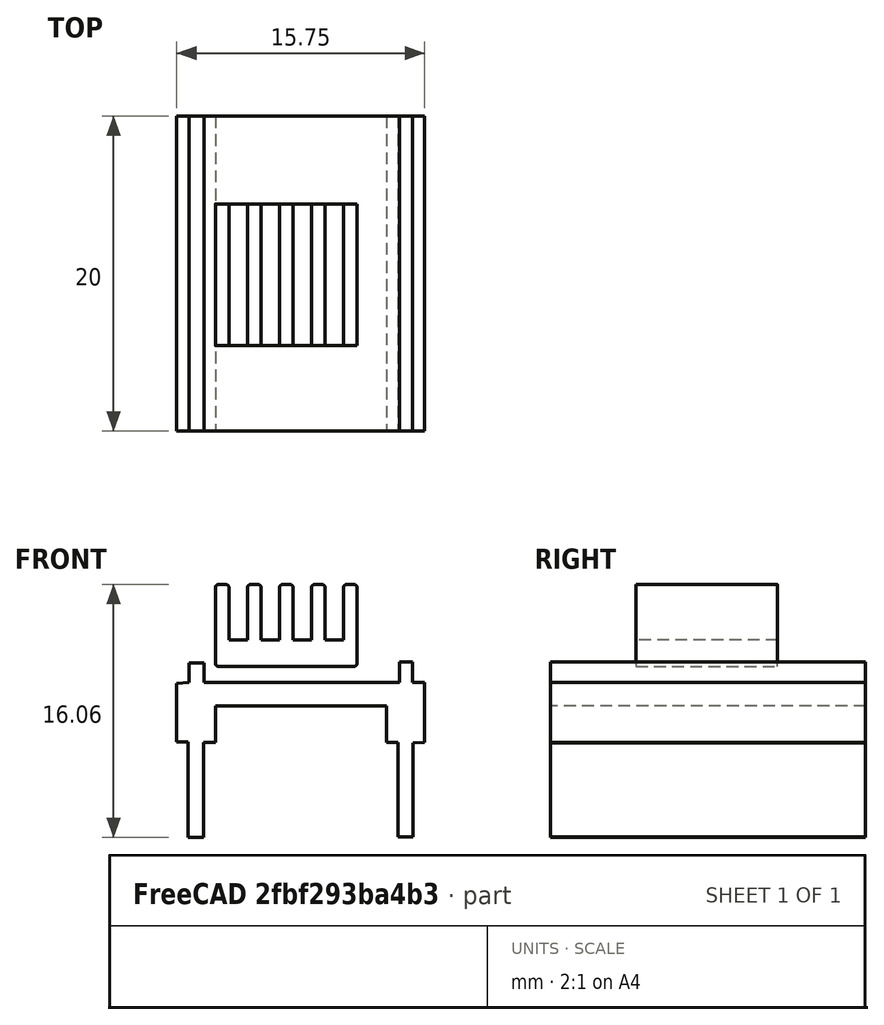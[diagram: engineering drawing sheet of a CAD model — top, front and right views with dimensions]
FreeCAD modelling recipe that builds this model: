
FCSTD DOCUMENT  (FreeCAD 0.16R6712 (Git))
Label: stepper
License: All rights reserved
LicenseURL: http://en.wikipedia.org/wiki/All_rights_reserved
objects: Part::Feature×1, Sketcher::SketchObject×1, PartDesign::Pad×1
note: 4 computed .brp shape members not serialized (recipe doc carries the construction recipe); baked Part::Feature solids carry a one-line shape summary decoded from their .brp

FEATURE [Part::Feature] Part__Feature034  label="Heat_Sink"
  Placement = pos=(-0.910921,-0.0804702,2.5) rot=(1,0,0;1.5708rad)
  shape: bbox 9 x 9 x 5.2 mm, 34 faces (baked)
FEATURE [Sketcher::SketchObject] Sketch
  Placement = pos=(0,0,0) rot=(-1,0,0;4.71239rad)
  sketch-geometry (25):
    g0: LineSegment StartX=-7.08984 StartY=2.70448 StartZ=0 EndX=-6.1315 EndY=2.70448 EndZ=0
    g1: LineSegment StartX=-6.1315 StartY=2.70448 StartZ=0 EndX=-6.1315 EndY=1.46643 EndZ=0
    g2: LineSegment StartX=-6.1315 StartY=1.46643 StartZ=0 EndX=6.27586 EndY=1.46643 EndZ=0
    g3: LineSegment StartX=6.27586 StartY=1.46643 StartZ=0 EndX=6.27586 EndY=2.77624 EndZ=0
    g4: LineSegment StartX=6.27586 StartY=2.77624 StartZ=0 EndX=7.1047 EndY=2.77624 EndZ=0
    g5: LineSegment StartX=7.1047 StartY=2.77624 StartZ=0 EndX=7.1047 EndY=1.47627 EndZ=0
    g6: LineSegment StartX=7.1047 StartY=1.47627 StartZ=0 EndX=7.8755 EndY=1.47627 EndZ=0
    g7: LineSegment StartX=7.8755 StartY=1.47627 StartZ=0 EndX=7.8755 EndY=-2.32364 EndZ=0
    g8: LineSegment StartX=7.8755 StartY=-2.32364 StartZ=0 EndX=7.12437 EndY=-2.36364 EndZ=0
    g9: LineSegment StartX=7.12437 StartY=-2.36364 StartZ=0 EndX=7.12437 EndY=-8.33415 EndZ=0
    g10: LineSegment StartX=7.12437 StartY=-8.33415 StartZ=0 EndX=6.19695 EndY=-8.31415 EndZ=0
    g11: LineSegment StartX=6.19695 StartY=-8.31415 StartZ=0 EndX=6.19695 EndY=-2.33428 EndZ=0
    g12: LineSegment StartX=6.19695 StartY=-2.33428 StartZ=0 EndX=5.44583 EndY=-2.33428 EndZ=0
    g13: LineSegment StartX=5.44583 StartY=-2.33428 StartZ=0 EndX=5.44583 EndY=0 EndZ=0
    g14: LineSegment StartX=5.44583 StartY=0 StartZ=0 EndX=-5.38959 EndY=0 EndZ=0
    g15: LineSegment StartX=-5.38959 StartY=0 StartZ=0 EndX=-5.38959 EndY=-2.33799 EndZ=0
    g16: LineSegment StartX=-5.38959 StartY=-2.33799 StartZ=0 EndX=-6.15088 EndY=-2.33799 EndZ=0
    g17: LineSegment StartX=-6.15088 StartY=-2.33799 StartZ=0 EndX=-6.15088 EndY=-8.35674 EndZ=0
    g18: LineSegment StartX=-6.15088 StartY=-8.35674 StartZ=0 EndX=-7.14748 EndY=-8.35674 EndZ=0
    g19: LineSegment StartX=-7.14748 StartY=-8.35674 StartZ=0 EndX=-7.14748 EndY=-2.30704 EndZ=0
    g20: LineSegment StartX=-7.14748 StartY=-2.30704 StartZ=0 EndX=-7.86844 EndY=-2.30704 EndZ=0
    g21: LineSegment StartX=-7.86844 StartY=-2.30704 StartZ=0 EndX=-7.86844 EndY=1.41435 EndZ=0
    g22: LineSegment StartX=-7.86844 StartY=1.41435 StartZ=0 EndX=-7.08172 EndY=1.46938 EndZ=0
    g23: LineSegment StartX=-7.08172 StartY=1.46938 StartZ=0 EndX=-7.08984 EndY=2.70448 EndZ=0
    g24: LineSegment StartX=-7.08984 StartY=2.70448 StartZ=0 EndX=-6.1315 EndY=2.70448 EndZ=0
  constraints (47):
    c: Coincident(g0,g1)
    c: Vertical(g1)
    c: Coincident(g1,g2)
    c: Horizontal(g2)
    c: Coincident(g2,g3)
    c: Vertical(g3)
    c: Coincident(g3,g4)
    c: Horizontal(g4)
    c: Coincident(g4,g5)
    c: Vertical(g5)
    c: Coincident(g5,g6)
    c: Horizontal(g6)
    c: Coincident(g6,g7)
    c: Vertical(g7)
    c: Coincident(g7,g8)
    c: Coincident(g8,g9)
    c: Vertical(g9)
    c: Coincident(g9,g10)
    c: Coincident(g10,g11)
    c: Vertical(g11)
    c: Coincident(g11,g12)
    c: Horizontal(g12)
    c: Coincident(g12,g13)
    c: PointOnObject(g13,g-1)
    c: Vertical(g13)
    c: Coincident(g13,g14)
    c: PointOnObject(g14,g-1)
    c: Coincident(g14,g15)
    c: Vertical(g15)
    c: Coincident(g15,g16)
    c: Horizontal(g16)
    c: Coincident(g16,g17)
    c: Vertical(g17)
    c: Coincident(g17,g18)
    c: Horizontal(g18)
    c: Coincident(g18,g19)
    c: Vertical(g19)
    c: Coincident(g19,g20)
    c: Horizontal(g20)
    c: Coincident(g20,g21)
    c: Vertical(g21)
    c: Coincident(g21,g22)
    c: Coincident(g22,g23)
    c: Coincident(g23,g0)
    c: Coincident(g23,g24)
    c: Coincident(g24,g0)
    c: Horizontal(g24)
FEATURE [PartDesign::Pad] Pad
  Length = 20
  Length2 = 100
  Midplane = true
  Placement = pos=(0,0,0) rot=(-1,0,0;4.71239rad)
  Sketch = -> Sketch
  Type = 0
